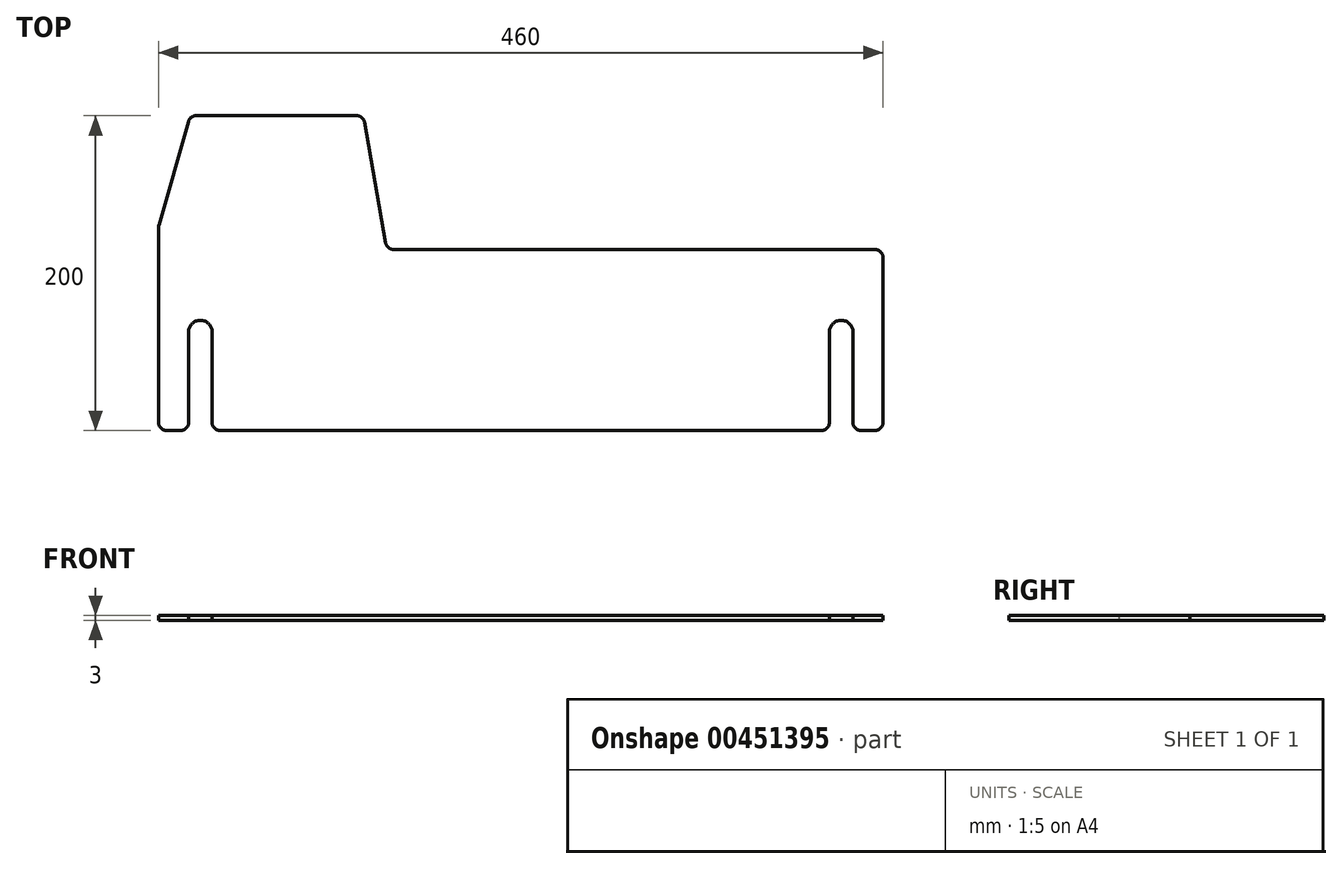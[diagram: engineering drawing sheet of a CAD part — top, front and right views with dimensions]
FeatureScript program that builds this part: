
annotation { "Feature Type Name" : "Feature", "Feature Type Description" : "" }
export const myFeature = defineFeature(function(context is Context, id is Id, definition is map)
    precondition{}
    {
        {
            var Q0;
            Q0=qCreatedBy(makeId("Top.planeOp"),FACE);
            var sketch = newSketch(context, id + "F0", { "sketchPlane" : qUnion([Q0])});
            skLineSegment(sketch, "E0.bottom", {"start": v(-210, 200) * mm, "end": v(-100, 200) * mm});
            skLineSegment(sketch, "E0.top", {"start": v(-230, 0) * mm, "end": v(-211, 0) * mm});
            skLineSegment(sketch, "E0.left", {"start": v(-230, 130) * mm, "end": v(-230, 0) * mm});
            skLineSegment(sketch, "E0.right", {"start": v(230, 115) * mm, "end": v(230, 0) * mm});
            skLineSegment(sketch, "E1.top", {"start": v(-85, 115) * mm, "end": v(230, 115) * mm});
            skLineSegment(sketch, "E2", {"start": v(-210, 200) * mm, "end": v(-230, 130) * mm});
            skLineSegment(sketch, "E3", {"start": v(-100, 200) * mm, "end": v(-85, 115) * mm});
            skPoint(sketch, "E1.left.start.orphan", {"position": v(-85, 200) * mm});
            skLineSegment(sketch, "E4.bottom", {"start": v(-203.5, 70) * mm, "end": v(-203.5, 70) * mm});
            skLineSegment(sketch, "E4.left", {"start": v(-211, 62.5) * mm, "end": v(-211, 0) * mm});
            skLineSegment(sketch, "E4.right", {"start": v(-196, 62.5) * mm, "end": v(-196, 0) * mm});
            skPoint(sketch, "E5.visualSharp", {"position": v(-211, 70) * mm});
            skArc(sketch, "E5.filletArc", {"start": v(-203.5, 70) * mm, "mid": v(-208.8, 67.8) * mm, "end": v(-211, 62.5) * mm});
            skPoint(sketch, "E6.visualSharp", {"position": v(-196, 70) * mm});
            skArc(sketch, "E6.filletArc", {"start": v(-196, 62.5) * mm, "mid": v(-198.2, 67.8) * mm, "end": v(-203.5, 70) * mm});
            skLineSegment(sketch, "E7.trimOffspring", {"start": v(-196, 0) * mm, "end": v(196, 0) * mm});
            skLineSegment(sketch, "E8.bottom", {"start": v(203.5, 70) * mm, "end": v(203.5, 70) * mm});
            skLineSegment(sketch, "E8.left", {"start": v(196, 62.5) * mm, "end": v(196, 0) * mm});
            skLineSegment(sketch, "E8.right", {"start": v(211, 62.5) * mm, "end": v(211, 0) * mm});
            skPoint(sketch, "E9.visualSharp", {"position": v(196, 70) * mm});
            skArc(sketch, "E9.filletArc", {"start": v(203.5, 70) * mm, "mid": v(198.2, 67.8) * mm, "end": v(196, 62.5) * mm});
            skPoint(sketch, "E10.visualSharp", {"position": v(211, 70) * mm});
            skArc(sketch, "E10.filletArc", {"start": v(211, 62.5) * mm, "mid": v(208.8, 67.8) * mm, "end": v(203.5, 70) * mm});
            skLineSegment(sketch, "E11.trimOffspring", {"start": v(211, 0) * mm, "end": v(230, 0) * mm});
            skSolve(sketch);
        }
        {
            var Q0;
            Q0=makeQuery(id+"F0.imprint","IMPRINT",FACE,{"disambiguationData":[TD([[makeQuery(id+"F0.imprint","IMPRINT",EDGE,{"derivedFrom":sQuery(id+"F0.wireOp",EDGE,"E0.bottom")}),-1.0]])]});
            extrude(context, id + "F1", {"entities" : qUnion([Q0]), "depth" : 3 * mm});
        }
        {
            var Q0;
            Q0=makeQuery(id+"F1.opExtrude","SWEPT_EDGE",EDGE,{"disambiguationData":[OSD([sQuery(id+"F0.wireOp",EDGE,"E0.top"),sQuery(id+"F0.wireOp",EDGE,"E4.left")])]});
            var Q1;
            Q1=makeQuery(id+"F1.opExtrude","SWEPT_EDGE",EDGE,{"disambiguationData":[OSD([sQuery(id+"F0.wireOp",EDGE,"E4.right"),sQuery(id+"F0.wireOp",EDGE,"E7.trimOffspring")])]});
            var Q2;
            Q2=makeQuery(id+"F1.opExtrude","SWEPT_EDGE",EDGE,{"disambiguationData":[OSD([sQuery(id+"F0.wireOp",EDGE,"E7.trimOffspring"),sQuery(id+"F0.wireOp",EDGE,"E8.left")])]});
            var Q3;
            Q3=makeQuery(id+"F1.opExtrude","SWEPT_EDGE",EDGE,{"disambiguationData":[OSD([sQuery(id+"F0.wireOp",EDGE,"E8.right"),sQuery(id+"F0.wireOp",EDGE,"E11.trimOffspring")])]});
            var Q4;
            Q4=makeQuery(id+"F1.opExtrude","SWEPT_EDGE",EDGE,{"disambiguationData":[OSD([sQuery(id+"F0.wireOp",EDGE,"E0.top"),sQuery(id+"F0.wireOp",EDGE,"E0.left")])]});
            var Q5;
            Q5=makeQuery(id+"F1.opExtrude","SWEPT_EDGE",EDGE,{"disambiguationData":[OSD([sQuery(id+"F0.wireOp",EDGE,"E0.left"),sQuery(id+"F0.wireOp",EDGE,"E2")])]});
            var Q6;
            Q6=makeQuery(id+"F1.opExtrude","SWEPT_EDGE",EDGE,{"disambiguationData":[OSD([sQuery(id+"F0.wireOp",EDGE,"E0.bottom"),sQuery(id+"F0.wireOp",EDGE,"E2")])]});
            var Q7;
            Q7=makeQuery(id+"F1.opExtrude","SWEPT_EDGE",EDGE,{"disambiguationData":[OSD([sQuery(id+"F0.wireOp",EDGE,"E0.bottom"),sQuery(id+"F0.wireOp",EDGE,"E3")])]});
            var Q8;
            Q8=makeQuery(id+"F1.opExtrude","SWEPT_EDGE",EDGE,{"disambiguationData":[OSD([sQuery(id+"F0.wireOp",EDGE,"E1.top"),sQuery(id+"F0.wireOp",EDGE,"E3")])]});
            var Q9;
            Q9=makeQuery(id+"F1.opExtrude","SWEPT_EDGE",EDGE,{"disambiguationData":[OSD([sQuery(id+"F0.wireOp",EDGE,"E0.right"),sQuery(id+"F0.wireOp",EDGE,"E1.top")])]});
            var Q10;
            Q10=makeQuery(id+"F1.opExtrude","SWEPT_EDGE",EDGE,{"disambiguationData":[OSD([sQuery(id+"F0.wireOp",EDGE,"E0.right"),sQuery(id+"F0.wireOp",EDGE,"E11.trimOffspring")])]});
            fillet(context, id + "F2", {"entities" : qUnion([Q0, Q1, Q2, Q3, Q4, Q5, Q6, Q7, Q8, Q9, Q10]), "radius" : 5 * mm, "tangentPropagation" : true, "allowEdgeOverflow" : false});
        }
    });
